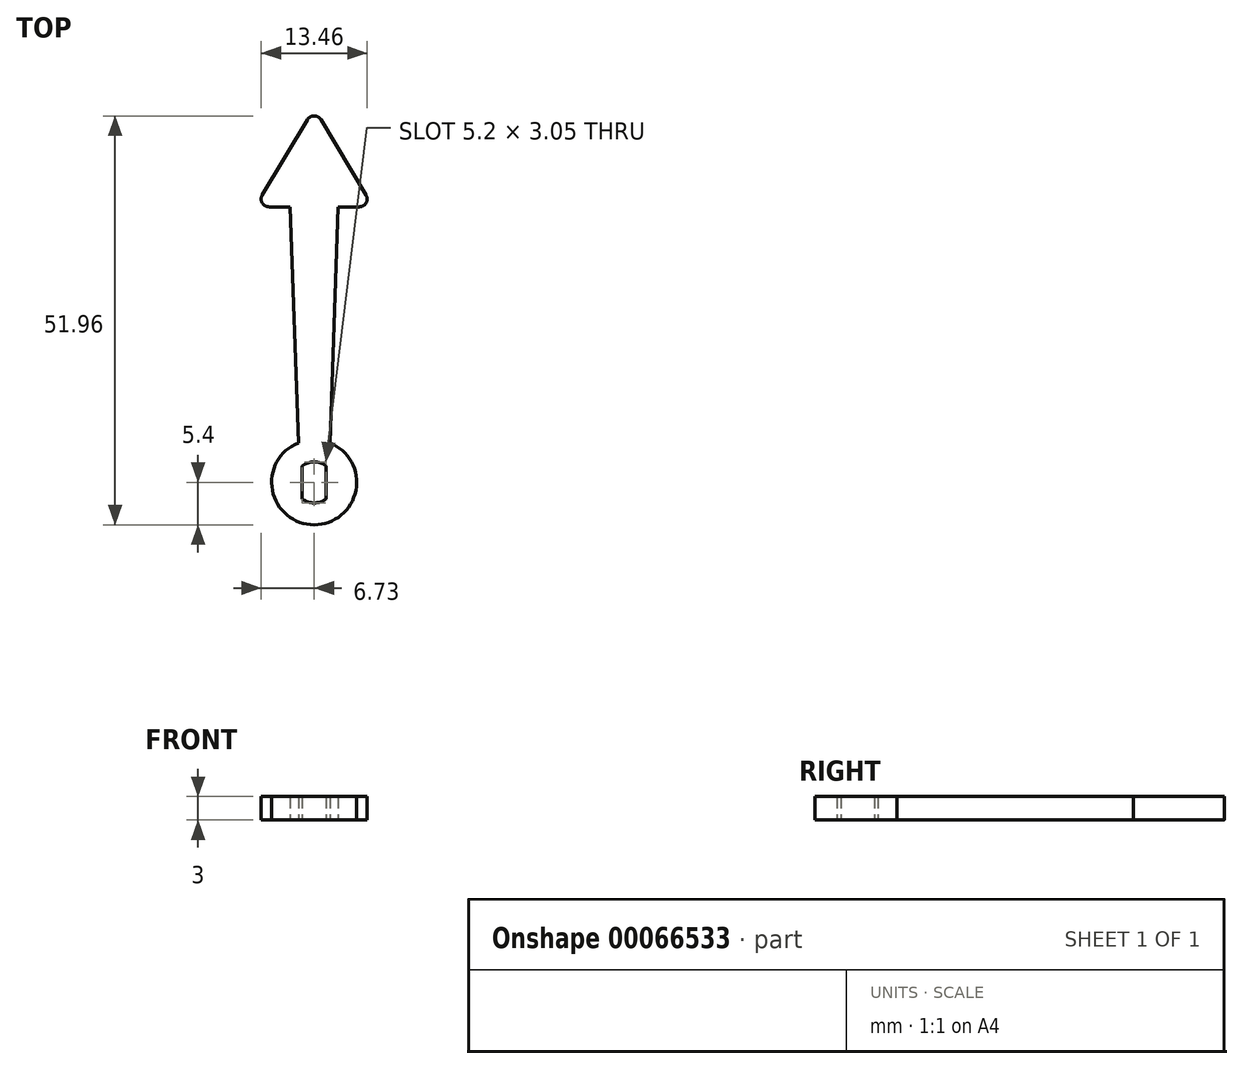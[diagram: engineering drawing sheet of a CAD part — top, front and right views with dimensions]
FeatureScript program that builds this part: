
annotation { "Feature Type Name" : "Feature", "Feature Type Description" : "" }
export const myFeature = defineFeature(function(context is Context, id is Id, definition is map)
    precondition{}
    {
        {
            var Q0;
            Q0=qCreatedBy(makeId("Top.planeOp"),FACE);
            var sketch = newSketch(context, id + "F0", { "sketchPlane" : qUnion([Q0])});
            skCircle(sketch, "E0", {"center": v(0, 0) * mm, "radius": 2.6 * mm});
            skCircle(sketch, "E1", {"center": v(0, 0) * mm, "radius": 5.4 * mm});
            skLineSegment(sketch, "E2", {"start": v(-1.53, 2.1) * mm, "end": v(-1.52, -2.1) * mm});
            skLineSegment(sketch, "E3", {"start": v(1.52, 2.1) * mm, "end": v(1.52, -2.1) * mm});
            skSolve(sketch);
        }
        {
            var Q0;
            {var subQ0=sQuery(id+"F0.wireOp",EDGE,"E3");Q0=makeQuery(id+"F0.imprint","IMPRINT",FACE,{"disambiguationData":[TD([[makeQuery(id+"F0.imprint","IMPRINT",EDGE,{"derivedFrom":subQ0}),1.0]])]});}
            var Q1;
            {var subQ0=sQuery(id+"F0.wireOp",EDGE,"E2");Q1=makeQuery(id+"F0.imprint","IMPRINT",FACE,{"disambiguationData":[TD([[makeQuery(id+"F0.imprint","IMPRINT",EDGE,{"derivedFrom":subQ0}),-1.0]])]});}
            var Q2;
            Q2=makeQuery(id+"F0.imprint","IMPRINT",FACE,{"disambiguationData":[TD([[makeQuery(id+"F0.imprint","IMPRINT",EDGE,{"derivedFrom":sQuery(id+"F0.wireOp",EDGE,"E1")}),1.0]])]});
            extrude(context, id + "F1", {"entities" : qUnion([Q0, Q1, Q2]), "endBound" : BoundingType.SYMMETRIC, "depth" : 3 * mm});
        }
        {
            var Q0;
            Q0=qCreatedBy(makeId("Top.planeOp"),FACE);
            var sketch = newSketch(context, id + "F2", { "sketchPlane" : qUnion([Q0])});
            skLineSegment(sketch, "E4", {"start": v(0, 0) * mm, "end": v(0, 35) * mm, "construction": true});
            skLineSegment(sketch, "E5", {"start": v(0, 4.72) * mm, "end": v(2, 4.72) * mm});
            skLineSegment(sketch, "E6", {"start": v(0, 35) * mm, "end": v(3.06, 35) * mm});
            skLineSegment(sketch, "E7", {"start": v(3.06, 35) * mm, "end": v(2, 4.72) * mm});
            skLineSegment(sketch, "E8.MirrorCS", {"start": v(0, 4.72) * mm, "end": v(-2, 4.72) * mm});
            skLineSegment(sketch, "E9.MirrorCS", {"start": v(-3.06, 35) * mm, "end": v(-2, 4.72) * mm});
            skLineSegment(sketch, "E10.MirrorCS", {"start": v(0, 35) * mm, "end": v(-3.06, 35) * mm});
            skSolve(sketch);
        }
        {
            var Q0;
            Q0=makeQuery(id+"F2.imprint","IMPRINT",FACE,{"disambiguationData":[TD([[makeQuery(id+"F2.imprint","IMPRINT",EDGE,{"derivedFrom":sQuery(id+"F2.wireOp",EDGE,"E5")}),1.0]])]});
            var Q1;
            Q1=makeQuery(id+"F1.opExtrude","CAP_FACE",FACE,{"disambiguationData":[OSD([sQuery(id+"F0.wireOp",EDGE,"E0"),sQuery(id+"F0.wireOp",EDGE,"E1"),sQuery(id+"F0.wireOp",EDGE,"E2"),sQuery(id+"F0.wireOp",EDGE,"E3")])],"isStart":false});
            extrude(context, id + "F3", {"entities" : qUnion([Q0]), "operationType" : NewBodyOperationType.ADD, "endBound" : BoundingType.UP_TO_SURFACE, "endBoundEntityFace" : qUnion([Q1]), "depth" : 25 * mm});
        }
        {
            var Q0;
            Q0=makeQuery(id+"F3.opExtrude","CAP_FACE",FACE,{"disambiguationData":[OSD([sQuery(id+"F2.wireOp",EDGE,"E5"),sQuery(id+"F2.wireOp",EDGE,"E6"),sQuery(id+"F2.wireOp",EDGE,"E7"),sQuery(id+"F2.wireOp",EDGE,"E8.MirrorCS"),sQuery(id+"F2.wireOp",EDGE,"E9.MirrorCS"),sQuery(id+"F2.wireOp",EDGE,"E10.MirrorCS")])],"isStart":true});
            var Q1;
            Q1=makeQuery(id+"F1.opExtrude","CAP_FACE",FACE,{"disambiguationData":[OSD([sQuery(id+"F0.wireOp",EDGE,"E0"),sQuery(id+"F0.wireOp",EDGE,"E1"),sQuery(id+"F0.wireOp",EDGE,"E2"),sQuery(id+"F0.wireOp",EDGE,"E3")])],"isStart":true});
            extrude(context, id + "F4", {"entities" : qUnion([Q0]), "operationType" : NewBodyOperationType.ADD, "endBound" : BoundingType.UP_TO_SURFACE, "endBoundEntityFace" : qUnion([Q1]), "depth" : 25 * mm});
        }
        {
            var Q0;
            Q0=qCreatedBy(makeId("Top.planeOp"),FACE);
            var sketch = newSketch(context, id + "F5", { "sketchPlane" : qUnion([Q0])});
            skLineSegment(sketch, "E11", {"start": v(0, 35) * mm, "end": v(0, 47.5) * mm, "construction": true});
            skLineSegment(sketch, "E12", {"start": v(-7.5, 35) * mm, "end": v(7.5, 35) * mm});
            skLineSegment(sketch, "E13", {"start": v(0, 47.5) * mm, "end": v(-7.5, 35) * mm});
            skLineSegment(sketch, "E14", {"start": v(0, 47.5) * mm, "end": v(7.5, 35) * mm});
            skSolve(sketch);
        }
        {
            var Q0;
            Q0=makeQuery(id+"F5.imprint","IMPRINT",FACE,{"disambiguationData":[TD([[makeQuery(id+"F5.imprint","IMPRINT",EDGE,{"derivedFrom":sQuery(id+"F5.wireOp",EDGE,"E12")}),1.0]])]});
            var Q1;
            Q1=makeQuery(id+"F3.boolean.opBoolean","MERGE",FACE,{"derivedFrom":[makeQuery(id+"F1.opExtrude","CAP_FACE",FACE,{"disambiguationData":[OSD([sQuery(id+"F0.wireOp",EDGE,"E0"),sQuery(id+"F0.wireOp",EDGE,"E1"),sQuery(id+"F0.wireOp",EDGE,"E2"),sQuery(id+"F0.wireOp",EDGE,"E3")])],"isStart":false}),makeQuery(id+"F3.opExtrude","CAP_FACE",FACE,{"disambiguationData":[OSD([sQuery(id+"F2.wireOp",EDGE,"E5"),sQuery(id+"F2.wireOp",EDGE,"E6"),sQuery(id+"F2.wireOp",EDGE,"E7"),sQuery(id+"F2.wireOp",EDGE,"E8.MirrorCS"),sQuery(id+"F2.wireOp",EDGE,"E9.MirrorCS"),sQuery(id+"F2.wireOp",EDGE,"E10.MirrorCS")])],"isStart":false})]});
            extrude(context, id + "F6", {"entities" : qUnion([Q0]), "operationType" : NewBodyOperationType.ADD, "endBound" : BoundingType.UP_TO_SURFACE, "endBoundEntityFace" : qUnion([Q1]), "depth" : 25 * mm});
        }
        {
            var Q0;
            Q0=makeQuery(id+"F6.opExtrude","CAP_FACE",FACE,{"disambiguationData":[OSD([sQuery(id+"F5.wireOp",EDGE,"E12"),sQuery(id+"F5.wireOp",EDGE,"E13"),sQuery(id+"F5.wireOp",EDGE,"E14")])],"isStart":true});
            var Q1;
            Q1=makeQuery(id+"F4.boolean.opBoolean","MERGE",FACE,{"derivedFrom":[makeQuery(id+"F1.opExtrude","CAP_FACE",FACE,{"disambiguationData":[OSD([sQuery(id+"F0.wireOp",EDGE,"E0"),sQuery(id+"F0.wireOp",EDGE,"E1"),sQuery(id+"F0.wireOp",EDGE,"E2"),sQuery(id+"F0.wireOp",EDGE,"E3")])],"isStart":true}),makeQuery(id+"F4.opExtrude","CAP_FACE",FACE,{"disambiguationData":[OSD([sQuery(id+"F2.wireOp",EDGE,"E5"),sQuery(id+"F2.wireOp",EDGE,"E6"),sQuery(id+"F2.wireOp",EDGE,"E7"),sQuery(id+"F2.wireOp",EDGE,"E8.MirrorCS"),sQuery(id+"F2.wireOp",EDGE,"E9.MirrorCS"),sQuery(id+"F2.wireOp",EDGE,"E10.MirrorCS")])],"isStart":false})]});
            extrude(context, id + "F7", {"entities" : qUnion([Q0]), "operationType" : NewBodyOperationType.ADD, "endBound" : BoundingType.UP_TO_SURFACE, "endBoundEntityFace" : qUnion([Q1]), "depth" : 25 * mm});
        }
        {
            var Q0;
            {var subQ0=sQuery(id+"F5.wireOp",EDGE,"E14");var subQ1=sQuery(id+"F5.wireOp",EDGE,"E13");Q0=makeQuery(id+"F7.boolean.opBoolean","MERGE",EDGE,{"derivedFrom":[makeQuery(id+"F6.opExtrude","SWEPT_EDGE",EDGE,{"disambiguationData":[OSD([subQ1,subQ0])]}),makeQuery(id+"F7.opExtrude","SWEPT_EDGE",EDGE,{"disambiguationData":[OSD([subQ1,subQ0])]})]});}
            var Q1;
            {var subQ0=sQuery(id+"F5.wireOp",EDGE,"E13");var subQ1=sQuery(id+"F5.wireOp",EDGE,"E12");Q1=makeQuery(id+"F7.boolean.opBoolean","MERGE",EDGE,{"derivedFrom":[makeQuery(id+"F6.opExtrude","SWEPT_EDGE",EDGE,{"disambiguationData":[OSD([subQ1,subQ0])]}),makeQuery(id+"F7.opExtrude","SWEPT_EDGE",EDGE,{"disambiguationData":[OSD([subQ1,subQ0])]})]});}
            var Q2;
            {var subQ0=sQuery(id+"F5.wireOp",EDGE,"E14");var subQ1=sQuery(id+"F5.wireOp",EDGE,"E12");Q2=makeQuery(id+"F7.boolean.opBoolean","MERGE",EDGE,{"derivedFrom":[makeQuery(id+"F6.opExtrude","SWEPT_EDGE",EDGE,{"disambiguationData":[OSD([subQ1,subQ0])]}),makeQuery(id+"F7.opExtrude","SWEPT_EDGE",EDGE,{"disambiguationData":[OSD([subQ1,subQ0])]})]});}
            fillet(context, id + "F8", {"entities" : qUnion([Q0, Q1, Q2]), "radius" : 1 * mm, "tangentPropagation" : true, "allowEdgeOverflow" : false});
        }
    });
